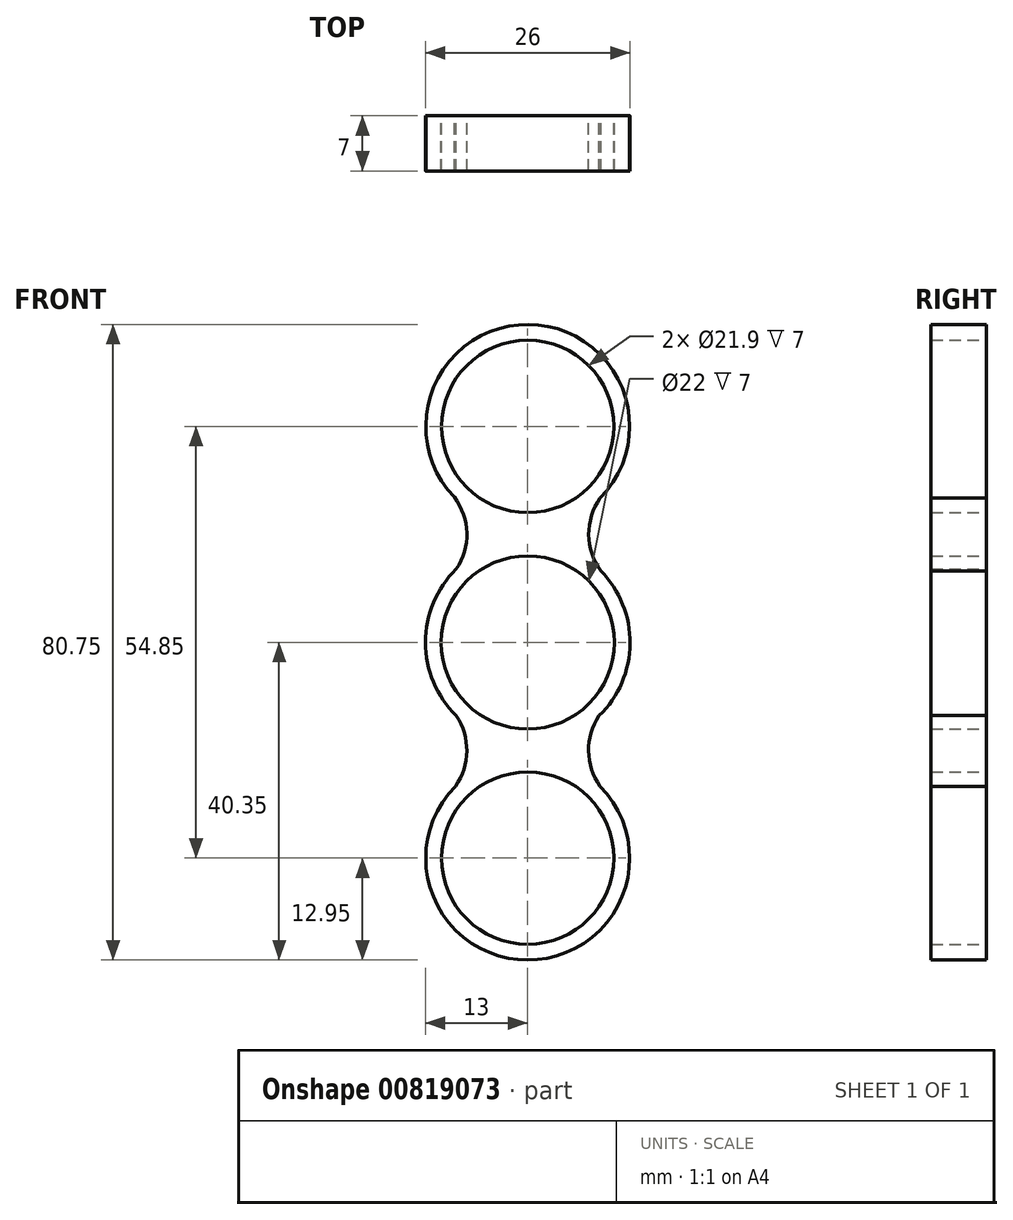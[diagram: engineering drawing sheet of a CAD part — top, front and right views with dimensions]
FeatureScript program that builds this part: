
annotation { "Feature Type Name" : "Feature", "Feature Type Description" : "" }
export const myFeature = defineFeature(function(context is Context, id is Id, definition is map)
    precondition{}
    {
        {
            var Q0;
            Q0=qCreatedBy(makeId("Front.planeOp"),FACE);
            var sketch = newSketch(context, id + "F0", { "sketchPlane" : qUnion([Q0])});
            skCircle(sketch, "E0", {"center": v(0, 0) * mm, "radius": 11 * mm});
            skCircle(sketch, "E1.0", {"center": v(0, 0) * mm, "radius": 13 * mm});
            skCircle(sketch, "E2", {"center": v(0, 27.45) * mm, "radius": 10.95 * mm});
            skCircle(sketch, "E3.0", {"center": v(0, 27.45) * mm, "radius": 12.95 * mm});
            skCircle(sketch, "E4.1.0", {"center": v(0, -27.4) * mm, "radius": 12.95 * mm});
            skCircle(sketch, "E4.1.1", {"center": v(0, -27.4) * mm, "radius": 10.95 * mm});
            skPoint(sketch, "E4.center", {"position": v(0, 0.02) * mm});
            skArc(sketch, "E5", {"start": v(10.27, 19.56) * mm, "mid": v(7.78, 14.52) * mm, "end": v(9.28, 9.1) * mm});
            skArc(sketch, "E6.MirrorCS", {"start": v(10.27, -19.51) * mm, "mid": v(7.77, -14.49) * mm, "end": v(9.24, -9.07) * mm});
            skArc(sketch, "E7.MirrorCS", {"start": v(-10.27, 19.51) * mm, "mid": v(-7.77, 14.49) * mm, "end": v(-9.24, 9.07) * mm});
            skArc(sketch, "E8.MirrorCS", {"start": v(-10.27, -19.51) * mm, "mid": v(-7.77, -14.49) * mm, "end": v(-9.24, -9.07) * mm});
            skSolve(sketch);
        }
        {
            var Q0;
            Q0 = qSketchRegion(id + "F0", true);
            extrude(context, id + "F1", {"entities" : qUnion([Q0]), "depth" : 7 * mm, "offsetDistance" : 25 * mm});
        }
    });
